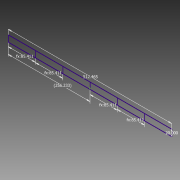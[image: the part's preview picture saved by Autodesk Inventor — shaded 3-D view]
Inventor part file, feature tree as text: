
AUTODESK INVENTOR PART (.ipt)
format: ipt  version: 2013 (Build 170138000, 138)  size: 68,096 bytes
history: native  units: in
note: dims shown in document units (in); Inventor stores cm internally (conversion verified against a paired STEP export)
features: sketch x1
ambient origin geometry x8: Origin, YZ Plane, XZ Plane, XY Plane, X Axis, Y Axis, Z Axis, Center Point
feature tree (1):
  sketch  "Sketch1"  dims[d0=512.465in d1=20.0in d2=256.2325in d3=85.4108in d4=85.4108in d5=85.4108in d6=85.4108in]
